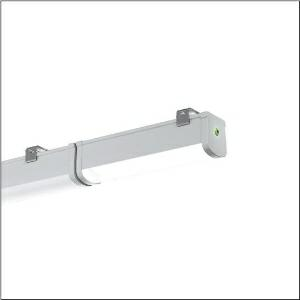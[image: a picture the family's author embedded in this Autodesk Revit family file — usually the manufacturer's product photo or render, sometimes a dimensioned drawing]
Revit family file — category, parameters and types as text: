
# Revit family: monsun_31_58fa207a403b3g
name_source: partatom
category: Lighting Fixtures
units: mm (PartAtom-declared; Revit-internal decimal feet)

## family parameters
Cut with Voids When Loaded = No
Host = Face
Light Source = No
Part Type = Normal
Room Calculation Point = No
Round Connector Dimension = Use Diameter
Shared = No

## types (1)
- --- (1 x LED, 450 lm, 5 W, 4000K)
    Apparent Load = 5 VA
    CIE Flux Codes = 42 72 91 92 100
    Color Rendering = 80
    Color Temperature = 4000K
    Default Elevation = 1800 mm
    Description = Monsun 31, emergency light element, primary optical cover: diffuser, of PC, frosted, light emission: direct distribution, primary light characteristic: symmetric, installation type: surface-mounted, EM-KIT 3h,LED, rated luminous flux: 450lm, luminous efficacy: 100lm/W, light colour: 840, colour temperature: 4000K, control gear: ON/OFF, emergency light function, with socket/plug, mains connection: 220..240V, AC, 50..60Hz, rated input power: 5W, housing, luminaire housing, of PC, light grey (RAL 7035), length: 297mm, width: 68mm, height: 76mm, protection rating (complete): IP65, insulation class (complete): insulation class II (safety insulation), certification: CE, protection symbol: D, impact resistance: IK08, permissible operating ambient temperature: 0..+40°C, standard: EN 60598-2-22, corresponds to IFS (International Featured Standards) requirements for safety and quality in the food industry, packaging unit: 1 piece
    Height = 77 mm
    Lamp = 1 x LED
    Lamp Light Flux = 450 lm
    Lamp Power = 5 W
    Lamp count = 1
    Length = 294 mm
    Luminous efficacy = 90 lm/W
    Manufacturer = Siteco
    ModVariant = No
    Model = 58FA207A403B3G
    Mounting Place = Ceiling
    Mounting Type = Surface mounted
    Number of Poles = 1
    OnlyDefault = Yes
    Power Factor = 1
    Product Name = Monsun 31
    Product group = emergency light element
    ProductGroupID = 309
    Protection Class = Protection class II
    Protection Degree = IP 65
    RLX_Detail_Level = 1
    RLX_Emergency_Light_Flux = 0 lm
    RLX_Emergency_Type = 0
    RLX_Emergency_Type_DB = No
    RlxData = <blob elided: 31033 chars, md5=14459fba>
    Socket = socket
    Standby Power = 0 W
    System Light Flux = 450 lm
    System Power = 5 W
    Type Comments = : 3 h
    Type Image = l_1006658.jpg
    URL = http://relux.com
    VarID = @adj_194983
    Voltage = 0 V
    Weight = 0.00 kg
    Width = 69 mm

## geometry (parser evidence)
native form markers: Blend x4, Sweep x10
no freeform markers — native parametric forms only
